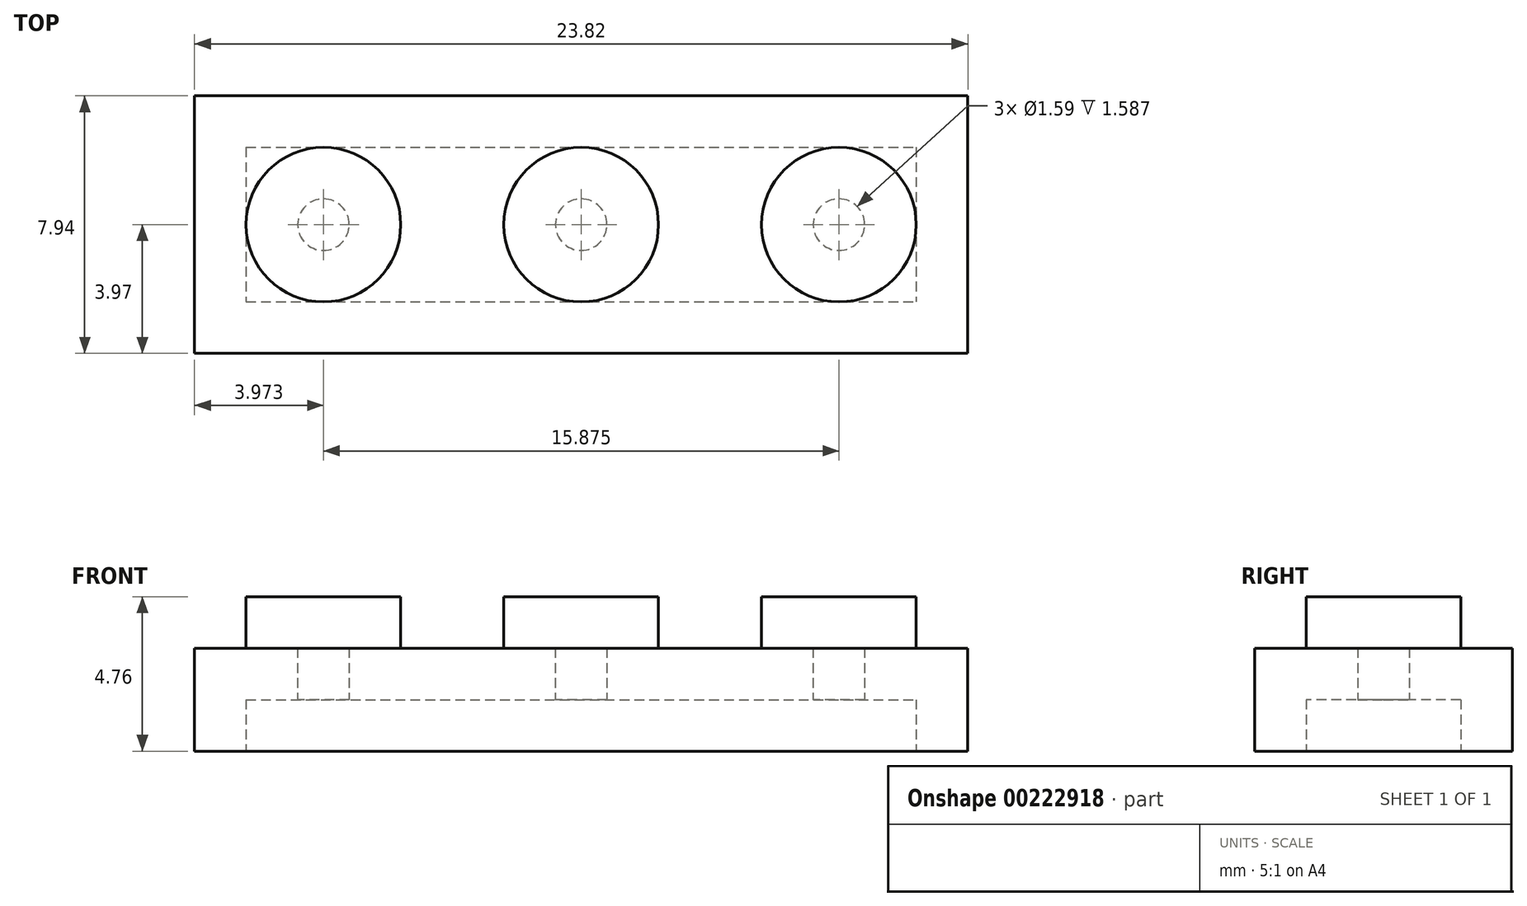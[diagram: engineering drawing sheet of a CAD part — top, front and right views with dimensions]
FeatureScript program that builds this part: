
annotation { "Feature Type Name" : "Feature", "Feature Type Description" : "" }
export const myFeature = defineFeature(function(context is Context, id is Id, definition is map)
    precondition{}
    {
        {
            var Q0;
            Q0=qCreatedBy(makeId("Top.planeOp"),FACE);
            var sketch = newSketch(context, id + "F0", { "sketchPlane" : qUnion([Q0])});
            skLineSegment(sketch, "E0.bottom", {"start": v(-11.9, 3.97) * mm, "end": v(11.9, 3.97) * mm});
            skLineSegment(sketch, "E0.top", {"start": v(-11.9, -3.97) * mm, "end": v(11.9, -3.97) * mm});
            skLineSegment(sketch, "E0.left", {"start": v(-11.9, 3.97) * mm, "end": v(-11.9, -3.97) * mm});
            skLineSegment(sketch, "E0.right", {"start": v(11.9, 3.97) * mm, "end": v(11.9, -3.97) * mm});
            skPoint(sketch, "E0.middle", {"position": v(0, 0) * mm});
            skCircle(sketch, "E1", {"center": v(-7.94, 0) * mm, "radius": 2.38 * mm});
            skCircle(sketch, "E2.1.0.0", {"center": v(0, 0) * mm, "radius": 2.38 * mm});
            skCircle(sketch, "E2.2.0.0", {"center": v(7.94, 0) * mm, "radius": 2.38 * mm});
            skLineSegment(sketch, "E2.direction1", {"start": v(-7.94, 0) * mm, "end": v(0, 0) * mm, "construction": true});
            skSolve(sketch);
        }
        {
            var Q0;
            Q0 = qSketchRegion(id + "F0", true);
            extrude(context, id + "F1", {"entities" : qUnion([Q0]), "depth" : 3.17 * mm});
        }
        {
            var Q0;
            Q0=makeQuery(id+"F0.imprint","IMPRINT",FACE,{"disambiguationData":[TD([[makeQuery(id+"F0.imprint","IMPRINT",EDGE,{"derivedFrom":sQuery(id+"F0.wireOp",EDGE,"E1")}),1.0]])]});
            var Q1;
            Q1=makeQuery(id+"F0.imprint","IMPRINT",FACE,{"disambiguationData":[TD([[makeQuery(id+"F0.imprint","IMPRINT",EDGE,{"derivedFrom":sQuery(id+"F0.wireOp",EDGE,"E2.1.0.0")}),1.0]])]});
            var Q2;
            Q2=makeQuery(id+"F0.imprint","IMPRINT",FACE,{"disambiguationData":[TD([[makeQuery(id+"F0.imprint","IMPRINT",EDGE,{"derivedFrom":sQuery(id+"F0.wireOp",EDGE,"E2.2.0.0")}),1.0]])]});
            extrude(context, id + "F2", {"entities" : qUnion([Q0, Q1, Q2]), "operationType" : NewBodyOperationType.ADD, "depth" : 4.76 * mm});
        }
        {
            var Q0;
            {var subQ0=sQuery(id+"F0.wireOp",EDGE,"E2.2.0.0");var subQ1=sQuery(id+"F0.wireOp",EDGE,"E2.1.0.0");var subQ2=sQuery(id+"F0.wireOp",EDGE,"E1");Q0=makeQuery(id+"F2.boolean.opBoolean","MERGE",FACE,{"derivedFrom":[makeQuery(id+"F1.opExtrude","CAP_FACE",FACE,{"disambiguationData":[OSD([sQuery(id+"F0.wireOp",EDGE,"E0.bottom"),sQuery(id+"F0.wireOp",EDGE,"E0.top"),sQuery(id+"F0.wireOp",EDGE,"E0.left"),sQuery(id+"F0.wireOp",EDGE,"E0.right"),subQ2,subQ1,subQ0])],"isStart":true}),makeQuery(id+"F2.opExtrude","CAP_FACE",FACE,{"disambiguationData":[OSD([subQ2])],"isStart":true}),makeQuery(id+"F2.opExtrude","CAP_FACE",FACE,{"disambiguationData":[OSD([subQ1])],"isStart":true}),makeQuery(id+"F2.opExtrude","CAP_FACE",FACE,{"disambiguationData":[OSD([subQ0])],"isStart":true})]});}
            shell(context, id + "F3", {"entities" : qUnion([Q0]), "thickness" : 1.59 * mm});
        }
    });
